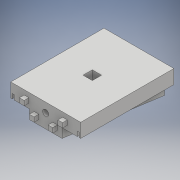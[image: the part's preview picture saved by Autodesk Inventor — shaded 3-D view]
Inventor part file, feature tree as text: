
AUTODESK INVENTOR PART (.ipt)
format: ipt  version: 2017 (Build 210142000, 142)  size: 199,168 bytes
history: native  units: mm
features: sketch x9, extrude x8, hole x1
ambient origin geometry x8: Origin, YZ Plane, XZ Plane, XY Plane, X Axis, Y Axis, Z Axis, Center Point
bodies: Body1 (feature_tree)
feature tree (18):
  extrude  "Extrusion2"  Depth=15.0mm
  hole  "Hole1"  [1 undecoded]
  extrude  "Extrusion11"  Depth=17.5mm
  extrude  "Extrusion12"  TaperAngle=90.0deg  [1 undecoded]
  extrude  "Extrusion13"  Depth=17.5mm
  extrude  "Extrusion16"  Depth=2.0mm
  extrude  "Extrusion17"  Depth=72.0mm
  extrude  "Extrusion20"  Depth=5.0mm TaperAngle=0.0deg
  extrude  "Extrusion21"  Depth=10.0mm
  sketch  "Sketch5"  dims[d6=75.0mm d7=15.0mm]
  sketch  "Sketch36"  dims[d8=100.0mm d9=0.0mm d82=10.0mm]
  sketch  "Sketch37"  dims[d83=6.4mm d84=6.0mm d85=4.0mm d86=2.0mm d87=90.0deg d88=10.0mm d89=20.594885mm d90=17.5mm]
  sketch  "Sketch38"  dims[d91=95.0mm d92=90.0deg]
  sketch  "Sketch39"  dims[d93=65.0mm d94=17.5mm]
  sketch  "Sketch43"  dims[d95=10.0mm d96=0.0mm d97=2.0mm]
  sketch  "Sketch45"  dims[d98=98.5mm d99=72.0mm]
  sketch  "Sketch48"  dims[d100=2.0mm d101=5.0mm d102=0.0mm]
  sketch  "Sketch49"  dims[d103=10.0mm d104=10.0mm d105=10.0mm d106=0.0mm d122=5.0mm d123=5.0mm d124=5.0mm d125=5.0mm d126=5.0mm d127=0.0mm d128=5.0mm d129=5.0mm d130=5.0mm d131=5.0mm d132=5.0mm d133=0.0mm d145=55.0mm d146=15.0mm d147=5.0mm d148=5.0mm d149=5.0mm d150=0.0mm d151=55.0mm d152=15.0mm d153=5.0mm d154=5.0mm d155=5.0mm d156=0.0mm]
note: 2 required parameter values undecoded (feature->parameter linkage not recoverable at this tier; creation-order binding heuristic only, values carry confidence <= 0.55)
